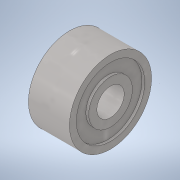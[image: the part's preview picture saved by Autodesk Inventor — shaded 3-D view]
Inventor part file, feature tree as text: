
AUTODESK INVENTOR PART (.ipt)
format: ipt  version: 2020 (Build 240168000, 168)  size: 134,656 bytes
history: native  units: mm
features: other x1, revolve x1, sketch x1
ambient origin geometry x8: Origin, YZ Plane, XZ Plane, XY Plane, X Axis, Y Axis, Z Axis, Center Point
bodies: Volumenkörper1 (feature_tree)
feature tree (3):
  other  "Kugellager 692-ZZ"
  revolve  "Umdrehung1"
  sketch  "Skizze1"  dims[d0=2.0mm d1=6.0mm d2=3.0mm d3=0.2mm d4=0.6mm d5=0.5mm d6=90.0deg]
